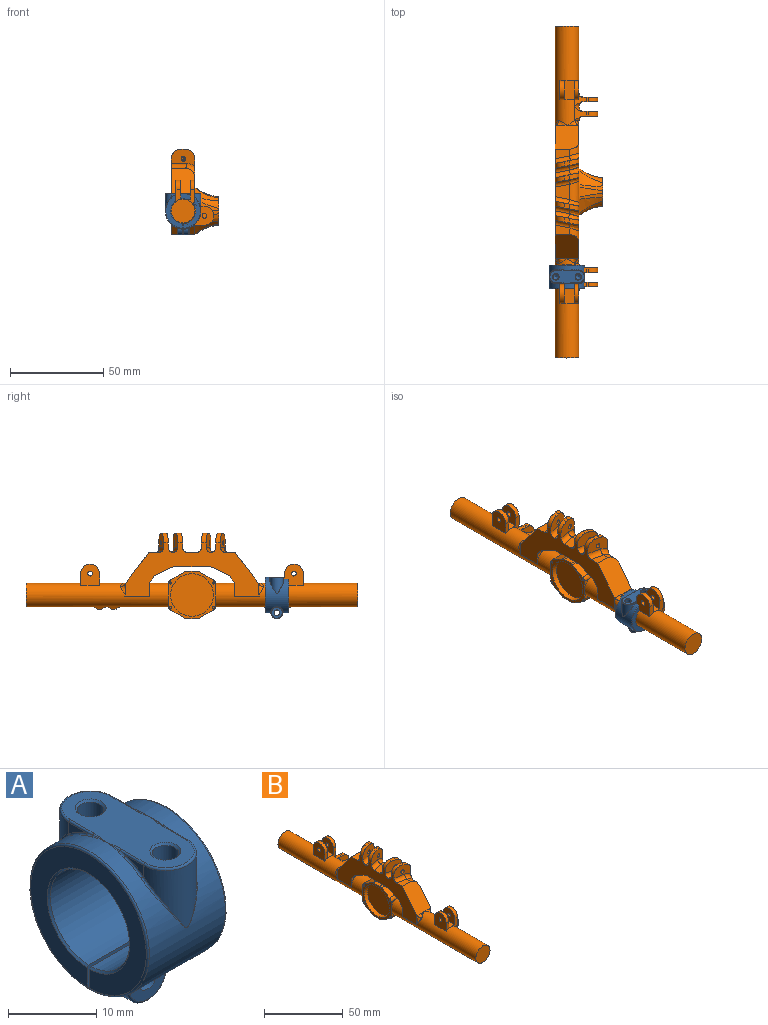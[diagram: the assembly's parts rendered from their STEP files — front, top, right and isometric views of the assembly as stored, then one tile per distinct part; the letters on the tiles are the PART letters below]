
ASSEMBLY  parts=2 mates=1
PART A: 89 faces, bbox 12.8x20.7x23.4 mm
  f0: cylinder r=9.53mm len=19.05mm, axis (-1,0,0), area 459.6mm2, adj f16,f17,f24,f25,f26,f27,f28,f29
  f1: cylinder r=6.35mm len=12.7mm, axis (-1,0,0), area 481.6mm2, adj f16,f17,f50,f51
  f2: cylinder r=1.5mm len=3mm, axis (0,1,0), area 28.1mm2, adj f10,f17
  f3: plane 18.54x18.54mm, normal (1,0,0), area 132mm2, adj f16,f17,f25,f51
  f4: plane 0.71x0.19mm, normal (-1,0,0), area 0.1mm2, adj f6,f20,f48
  f5: plane 0.71x0.19mm, normal (1,0,0), area 0.1mm2, adj f6,f18,f40
  f6: cylinder r=3.17mm len=6.35mm, axis (0,1,0), area 26.7mm2, adj f4,f5,f17,f19,f39,f49
  f7: cylinder r=1.5mm len=3mm, axis (0,1,0), area 28.1mm2, adj f9,f16
  f8: plane 18.54x18.54mm, normal (-1,0,0), area 132mm2, adj f16,f17,f24,f50
  f9: plane 5.84x5.84mm, normal (0,-1,0), area 19.8mm2, adj f7,f21,f22,f23,f32,f33,f34
  f10: plane 5.84x5.84mm, normal (0,1,0), area 19.8mm2, adj f2,f18,f19,f20,f43,f44,f45
  f11: cylinder r=3.17mm len=6.35mm, axis (0,1,0), area 26.7mm2, adj f12,f13,f16,f22,f28,f38
  f12: plane 0.71x0.19mm, normal (-1,0,0), area 0.1mm2, adj f11,f23,f29
  f13: plane 0.71x0.19mm, normal (1,0,0), area 0.1mm2, adj f11,f21,f37
  f14: cylinder r=3.17mm len=6.12mm, axis (0,-1,0), area 21mm2, adj f27,f44
  f15: cylinder r=3.17mm len=6.12mm, axis (0,1,0), area 21mm2, adj f26,f33
  f16: plane 12.71x6.36mm, normal (0,1,0), area 49mm2, adj f0,f1,f3,f7,f8,f11,f24,f25
  f17: plane 12.71x6.36mm, normal (0,-1,0), area 49mm2, adj f0,f1,f2,f3,f6,f8,f24,f25
  f18: cylinder r=0.25mm len=0.57mm, axis (0,0,-1), area 0.1mm2, adj f5,f10,f19,f41,f42
  f19: torus R=2.92mm, axis (0,-1,0), area 3.9mm2, adj f6,f10,f18,f20
  f20: cylinder r=0.25mm len=0.57mm, axis (0,0,1), area 0.1mm2, adj f4,f10,f19,f46,f47
  f21: cylinder r=0.25mm len=0.57mm, axis (0,0,1), area 0.1mm2, adj f9,f13,f22,f35,f36
  f22: torus R=2.92mm, axis (0,-1,0), area 3.9mm2, adj f9,f11,f21,f23
  f23: cylinder r=0.25mm len=0.57mm, axis (0,0,-1), area 0.1mm2, adj f9,f12,f22,f30,f31
  f24: torus R=9.27mm, axis (1,0,0), area 23.5mm2, adj f0,f8,f16,f17
  f25: torus R=9.27mm, axis (-1,0,0), area 23.5mm2, adj f0,f3,f16,f17
  f26: bspline ~6.77x5.02mm, area 3.3mm2, adj f0,f15,f31,f32,f34,f35
  f27: bspline ~6.77x5.02mm, area 3.3mm2, adj f0,f14,f42,f43,f45,f46
  f28: bspline ~3.57x0.71mm, area 0.8mm2, adj f0,f11,f16,f29
  f29: torus R=9.78mm, axis (-1,0,0), area 0.3mm2, adj f0,f12,f28,f30
  f30: bspline ~0.39x0.37mm, area 0.1mm2, adj f0,f23,f29,f31
  f31: bspline ~0.47x0.45mm, area 0.1mm2, adj f23,f26,f30,f32
  f32: bspline ~0.38x0.33mm, area 0.1mm2, adj f9,f26,f31,f33
  f33: torus R=2.92mm, axis (0,-1,0), area 3.2mm2, adj f9,f15,f32,f34
  f34: bspline ~0.38x0.35mm, area 0.1mm2, adj f9,f26,f33,f35
  f35: bspline ~0.49x0.46mm, area 0.1mm2, adj f21,f26,f34,f36
  f36: bspline ~0.41x0.38mm, area 0.1mm2, adj f0,f21,f35,f37
  f37: torus R=9.78mm, axis (-1,0,0), area 0.3mm2, adj f0,f13,f36,f38
  f38: bspline ~3.57x0.71mm, area 0.8mm2, adj f0,f11,f16,f37
  f39: bspline ~3.57x0.71mm, area 0.8mm2, adj f0,f6,f17,f40
  f40: torus R=9.78mm, axis (-1,0,0), area 0.3mm2, adj f0,f5,f39,f41
  f41: bspline ~0.39x0.37mm, area 0.1mm2, adj f0,f18,f40,f42
  f42: bspline ~0.47x0.45mm, area 0.1mm2, adj f18,f27,f41,f43
  f43: bspline ~0.38x0.35mm, area 0.1mm2, adj f10,f27,f42,f44
  f44: torus R=2.92mm, axis (0,-1,0), area 3.2mm2, adj f10,f14,f43,f45
  f45: bspline ~0.38x0.33mm, area 0.1mm2, adj f10,f27,f44,f46
  f46: bspline ~0.49x0.46mm, area 0.1mm2, adj f20,f27,f45,f47
  f47: bspline ~0.41x0.38mm, area 0.1mm2, adj f0,f20,f46,f48
  f48: torus R=9.78mm, axis (-1,0,0), area 0.3mm2, adj f0,f4,f47,f49
  f49: bspline ~3.57x0.71mm, area 0.8mm2, adj f0,f6,f17,f48
  f50: cone r=6.35mm half-angle=45deg, axis (-1,0,0), area 14.5mm2, adj f1,f8,f16,f17
  f51: cone r=6.6mm half-angle=45deg, axis (1,0,0), area 14.5mm2, adj f1,f3,f16,f17
  f52: plane 2.89x1.55mm, normal (1,0,0), area 1.9mm2, adj f53,f62,f80
  f53: cylinder r=3.5mm len=8.58mm, axis (0,0,1), area 53.7mm2, adj f52,f54,f63,f79
  f54: plane 2.89x1.55mm, normal (-1,0,0), area 1.9mm2, adj f53,f61,f78
  f55: cylinder r=3.5mm len=8.58mm, axis (0,0,1), area 53.7mm2, adj f56,f57,f66,f72
  f56: plane 2.89x1.55mm, normal (-1,0,0), area 1.9mm2, adj f55,f65,f73
  f57: plane 2.89x1.55mm, normal (1,0,0), area 1.9mm2, adj f55,f67,f71
  f58: plane 18.58x7.09mm, normal (0,0,1), area 92.5mm2, adj f59,f60,f61,f62,f63,f64,f65,f66
  f59: bspline ~2.28x0.28mm, area 0.2mm2, adj f58,f61,f76
  f60: bspline ~2.28x0.28mm, area 0.2mm2, adj f58,f62,f82
  f61: cylinder r=0.25mm len=3.82mm, axis (0,-1,0), area 1.5mm2, adj f54,f58,f59,f63,f77
  f62: cylinder r=0.25mm len=3.82mm, axis (0,1,0), area 1.5mm2, adj f52,f58,f60,f63,f81
  f63: torus R=3.25mm, axis (0,0,1), area 4.3mm2, adj f53,f58,f61,f62
  f64: bspline ~2.28x0.28mm, area 0.2mm2, adj f58,f65,f75
  f65: cylinder r=0.25mm len=3.82mm, axis (0,-1,0), area 1.5mm2, adj f56,f58,f64,f66,f74
  f66: torus R=3.25mm, axis (0,0,1), area 4.3mm2, adj f55,f58,f65,f67
  f67: cylinder r=0.25mm len=3.82mm, axis (0,1,0), area 1.5mm2, adj f57,f58,f66,f68,f70
  f68: bspline ~2.28x0.28mm, area 0.2mm2, adj f58,f67,f69
  f69: bspline ~2.19x0.24mm, area 0.2mm2, adj f0,f68,f70
  f70: bspline ~1.88x0.52mm, area 0.3mm2, adj f0,f67,f69,f71
  f71: torus R=9.78mm, axis (1,0,0), area 1.3mm2, adj f0,f57,f70,f72
  f72: bspline ~7.61x7.51mm, area 3.8mm2, adj f0,f55,f71,f73
  f73: torus R=9.78mm, axis (1,0,0), area 1.3mm2, adj f0,f56,f72,f74
  f74: bspline ~2.13x0.61mm, area 0.3mm2, adj f0,f65,f73,f75
  f75: bspline ~2.19x0.24mm, area 0.3mm2, adj f0,f64,f74
  f76: bspline ~2.36x0.28mm, area 0.2mm2, adj f0,f59,f77
  f77: bspline ~2.13x0.61mm, area 0.3mm2, adj f0,f61,f76,f78
  f78: torus R=9.78mm, axis (1,0,0), area 1.3mm2, adj f0,f54,f77,f79
  f79: bspline ~7.61x7.51mm, area 3.8mm2, adj f0,f53,f78,f80
  f80: torus R=9.78mm, axis (1,0,0), area 1.3mm2, adj f0,f52,f79,f81
  f81: bspline ~1.88x0.52mm, area 0.3mm2, adj f0,f62,f80,f82
  f82: bspline ~2.53x0.33mm, area 0.2mm2, adj f0,f60,f81
  f83: cone r=0mm half-angle=59deg, axis (0,0,1), area 8.2mm2, adj f84
  f84: cylinder r=1.5mm len=3mm, axis (0,0,1), area 27.5mm2, adj f83,f88
  f85: cone r=0mm half-angle=59deg, axis (0,0,1), area 8.2mm2, adj f86
  f86: cylinder r=1.5mm len=3mm, axis (0,0,1), area 27.5mm2, adj f85,f87
  f87: cone r=1.5mm half-angle=45deg, axis (0,0,1), area 3.7mm2, adj f58,f86
  f88: cone r=1.5mm half-angle=45deg, axis (0,0,1), area 3.7mm2, adj f58,f84
PART B: 219 faces, bbox 28.6x179.7x47.6 mm
  f0: cylinder r=6.35mm len=76.2mm, axis (0,-1,0), area 2387mm2, adj f1,f2,f3,f10,f24,f25,f26,f30
  f1: plane 7.45x6.35mm, normal (0,-1,0), area 19.1mm2, adj f0,f10,f195,f203,f204,f205,f213
  f2: plane 7.62x6.35mm, normal (0,1,0), area 19.2mm2, adj f0,f195,f203,f204,f205,f213
  f3: plane 6.35x3.81mm, normal (0,1,0), area 14.4mm2, adj f0,f194,f202,f204,f207
  f4: plane 7.45x6.35mm, normal (0,1,0), area 19.1mm2, adj f7,f8,f198,f200,f201,f206,f214
  f5: plane 6.35x3.81mm, normal (0,1,0), area 14.4mm2, adj f7,f197,f199,f201,f208
  f6: plane 7.62x6.35mm, normal (0,-1,0), area 19.2mm2, adj f7,f198,f200,f201,f206,f214
  f7: cylinder r=6.35mm len=76.2mm, axis (0,-1,0), area 2387mm2, adj f4,f5,f6,f8,f9,f21,f22,f23
  f8: cylinder r=10.16mm len=6.49mm, axis (0,-1,0), area 24.3mm2, adj f4,f7,f9,f124,f125,f126,f191,f214
  f9: torus R=8.89mm, axis (0,-1,0), area 54.5mm2, adj f7,f8,f126,f141,f214
  f10: cylinder r=10.16mm len=6.49mm, axis (0,-1,0), area 24.3mm2, adj f0,f1,f131,f133,f134,f188,f189,f213
  f11: plane 7.62x1.53mm, normal (0,0,1), area 0mm2, adj f78,f150,f180,f184
  f12: plane 7.62x5.14mm, normal (0,0,1), area 33.4mm2, adj f78,f89,f153,f172
  f13: plane 7.62x1.53mm, normal (0,0,1), area 0mm2, adj f78,f152,f176,f186
  f14: plane 7.62x5.14mm, normal (0,0,1), area 33.4mm2, adj f78,f88,f151,f174
  f15: plane 8.13x7.62mm, normal (0,0,1), area 50.3mm2, adj f78,f149,f178,f182
  f16: cylinder r=0.64mm len=5.08mm, axis (-1,0,0), area 9.3mm2, adj f20,f63,f71
  f17: cylinder r=0.64mm len=5.08mm, axis (-1,0,0), area 9.3mm2, adj f20,f64,f70
  f18: cylinder r=0.64mm len=5.08mm, axis (-1,0,0), area 9.3mm2, adj f20,f65,f69
  f19: cylinder r=0.64mm len=5.08mm, axis (-1,0,0), area 9.3mm2, adj f20,f66,f68
  f20: plane 25.4x25.4mm, normal (-1,0,0), area 129.2mm2, adj f16,f17,f18,f19,f21,f22,f24,f25
  f21: plane 5.87x3.92mm, normal (0,-1,0), area 6.4mm2, adj f7,f20,f42
  f22: plane 5.87x3.92mm, normal (0,-1,0), area 6.4mm2, adj f7,f20,f35
  f23: plane 5.97x4.02mm, normal (0,-1,0), area 6.4mm2, adj f7,f35,f54
  f24: plane 5.87x3.92mm, normal (0,1,0), area 6.4mm2, adj f0,f20,f40
  f25: plane 5.87x3.92mm, normal (0,1,0), area 6.4mm2, adj f0,f20,f38
  f26: plane 5.93x3.98mm, normal (0,1,0), area 6.4mm2, adj f0,f38,f49
  f27: plane 12.72x5.47mm, normal (0,0,1), area 69.1mm2, adj f20,f39,f41,f59
  f28: plane 5.93x3.98mm, normal (0,-1,0), area 6.4mm2, adj f7,f42,f56
  f29: plane 12.72x5.47mm, normal (0,0,-1), area 69.1mm2, adj f20,f36,f37,f46
  f30: plane 5.97x4.02mm, normal (0,1,0), area 6.4mm2, adj f0,f40,f51
  f31: plane 12.82x7.56mm, normal (0,-0.5,0.87), area 109.1mm2, adj f20,f41,f42,f60
  f32: plane 12.79x7.53mm, normal (0,0.5,0.87), area 109.1mm2, adj f20,f39,f40,f55
  f33: plane 12.82x7.56mm, normal (0,0.5,-0.87), area 109.1mm2, adj f20,f37,f38,f45
  f34: plane 12.79x7.53mm, normal (0,-0.5,-0.87), area 109.1mm2, adj f20,f35,f36,f50
  f35: cylinder r=2.54mm len=12.7mm, axis (1,0,0), area 32.2mm2, adj f7,f20,f22,f23,f34,f52
  f36: cylinder r=2.54mm len=12.7mm, axis (1,0,0), area 16.9mm2, adj f20,f29,f34,f48
  f37: cylinder r=2.54mm len=12.7mm, axis (1,0,0), area 16.9mm2, adj f20,f29,f33,f44
  f38: cylinder r=2.54mm len=12.7mm, axis (-1,0,0), area 32.2mm2, adj f0,f20,f25,f26,f33,f47
  f39: cylinder r=2.54mm len=12.7mm, axis (-1,0,0), area 16.9mm2, adj f20,f27,f32,f57
  f40: cylinder r=2.54mm len=12.7mm, axis (-1,0,0), area 32.2mm2, adj f0,f20,f24,f30,f32,f53
  f41: cylinder r=2.54mm len=12.7mm, axis (-1,0,0), area 16.9mm2, adj f20,f27,f31,f61
  f42: cylinder r=2.54mm len=12.7mm, axis (1,0,0), area 32.2mm2, adj f7,f20,f21,f28,f31,f58
  f43: plane 15.29x15.27mm, normal (1,0,0), area 136.8mm2, adj f44,f45,f46,f47,f48,f49,f50,f51
  f44: bspline ~12.7x5.81mm, area 24.7mm2, adj f37,f43,f45,f46
  f45: bspline ~12.7x8.64mm, area 72.1mm2, adj f33,f43,f44,f47
  f46: bspline ~12.7x5.44mm, area 45.7mm2, adj f29,f43,f44,f48
  f47: bspline ~12.7x7.77mm, area 48.9mm2, adj f38,f43,f45,f49
  f48: bspline ~12.7x5.81mm, area 24.7mm2, adj f36,f43,f46,f50
  f49: bspline ~12.7x5.87mm, area 49.3mm2, adj f26,f43,f47,f51
  f50: bspline ~12.7x8.64mm, area 72.1mm2, adj f34,f43,f48,f52
  f51: bspline ~12.7x5.87mm, area 49.3mm2, adj f30,f43,f49,f53
  f52: bspline ~12.7x7.77mm, area 48.9mm2, adj f35,f43,f50,f54
  f53: bspline ~12.7x7.77mm, area 48.9mm2, adj f40,f43,f51,f55
  f54: bspline ~12.7x5.87mm, area 49.3mm2, adj f23,f43,f52,f56
  f55: bspline ~12.7x8.64mm, area 72.1mm2, adj f32,f43,f53,f57
  f56: bspline ~12.7x5.87mm, area 49.3mm2, adj f28,f43,f54,f58
  f57: bspline ~12.7x5.81mm, area 24.7mm2, adj f39,f43,f55,f59
  f58: bspline ~12.7x7.77mm, area 48.9mm2, adj f42,f43,f56,f60
  f59: bspline ~12.7x5.44mm, area 45.7mm2, adj f27,f43,f57,f61
  f60: bspline ~12.7x8.64mm, area 72.1mm2, adj f31,f43,f58,f61
  f61: bspline ~12.7x5.81mm, area 24.7mm2, adj f41,f43,f59,f60
  f62: cylinder r=3.81mm len=7.62mm, axis (1,0,0), area 121.6mm2, adj f43,f215
  f63: plane 1.26x1.1mm, normal (-1,0,0), area 1.1mm2, adj f16,f71
  f64: plane 1.26x1.1mm, normal (-1,0,0), area 1.1mm2, adj f17,f70
  f65: plane 1.26x1.1mm, normal (-1,0,0), area 1.1mm2, adj f18,f69
  f66: plane 1.26x1.1mm, normal (-1,0,0), area 1.1mm2, adj f19,f68
  f67: cylinder r=11.43mm len=22.86mm, axis (-1,0,0), area 220.7mm2, adj f20,f216
  f68: cylinder r=0.64mm len=5.08mm, axis (-1,0,0), area 9.3mm2, adj f19,f20,f66
  f69: cylinder r=0.64mm len=5.08mm, axis (-1,0,0), area 9.3mm2, adj f18,f20,f65
  f70: cylinder r=0.64mm len=5.08mm, axis (-1,0,0), area 9.3mm2, adj f17,f20,f64
  f71: cylinder r=0.64mm len=5.08mm, axis (-1,0,0), area 9.3mm2, adj f16,f20,f63
  f72: plane 0.13x0.13mm, normal (0,1,0), area 0mm2, adj f78,f88,f164
  f73: plane 0.13x0.13mm, normal (0,1,0), area 0mm2, adj f79,f88,f161
  f74: plane 0.64x0.03mm, normal (0,-1,0), area 0mm2, adj f0,f78,f94
  f75: plane 6.35x6.35mm, normal (0,-1,0), area 8.7mm2, adj f0,f78,f87
  f76: plane 6.35x6.35mm, normal (0,-1,0), area 8.7mm2, adj f0,f79,f87
  f77: plane 13.25x0.11mm, normal (0,0,-1), area 0.4mm2, adj f0,f79,f93,f156
  f78: plane 73.11x30.44mm, normal (-1,0,0), area 891.6mm2, adj f11,f12,f13,f14,f15,f72,f74,f75
  f79: plane 72.3x29.63mm, normal (1,0,0), area 722.1mm2, adj f73,f76,f77,f82,f84,f85,f86,f87
  f80: plane 0.64x0.03mm, normal (0,1,0), area 0mm2, adj f7,f78,f92
  f81: plane 6.35x6.35mm, normal (0,1,0), area 8.7mm2, adj f7,f78,f90
  f82: plane 6.35x6.35mm, normal (0,1,0), area 8.7mm2, adj f7,f79,f90
  f83: plane 0.13x0.13mm, normal (0,-1,0), area 0mm2, adj f78,f89,f170
  f84: plane 0.13x0.13mm, normal (0,-1,0), area 0mm2, adj f79,f89,f167
  f85: plane 13.25x0.11mm, normal (0,0,-1), area 0.4mm2, adj f7,f79,f91,f158
  f86: plane 19.47x12.7mm, normal (0,0,-1), area 247.2mm2, adj f78,f79,f95,f96
  f87: plane 12.7x3.86mm, normal (0,-0.79,-0.61), area 61.8mm2, adj f75,f76,f78,f79,f95
  f88: plane 18.38x14.57mm, normal (0,0.79,0.61), area 257.5mm2, adj f14,f72,f73,f78,f79,f151,f162,f163
  f89: plane 18.38x14.57mm, normal (0,-0.79,0.61), area 257.5mm2, adj f12,f78,f79,f83,f84,f153,f168,f169
  f90: plane 12.7x3.86mm, normal (0,0.79,-0.61), area 61.8mm2, adj f78,f79,f81,f82,f96
  f91: plane 0.64x0.03mm, normal (0,1,0), area 0mm2, adj f7,f79,f85
  f92: plane 13.25x0.11mm, normal (0,0,-1), area 0.4mm2, adj f7,f78,f80,f159
  f93: plane 0.64x0.03mm, normal (0,-1,0), area 0mm2, adj f0,f77,f79
  f94: plane 13.25x0.11mm, normal (0,0,-1), area 0.4mm2, adj f0,f74,f78,f157
  f95: plane 12.7x10.22mm, normal (0,-0.44,-0.9), area 144.7mm2, adj f78,f79,f86,f87
  f96: plane 12.7x10.22mm, normal (0,0.44,-0.9), area 144.7mm2, adj f78,f79,f86,f90
  f97: plane 13.13x10.54mm, normal (0.2,-0.98,0), area 87.3mm2, adj f78,f79,f99,f109,f110,f118,f178,f179
  f98: plane 13.13x9.65mm, normal (-0.2,0.98,0), area 85.3mm2, adj f78,f79,f99,f109,f110,f118,f176,f177
  f99: plane 3.05x2.54mm, normal (0,0,1), area 6.5mm2, adj f97,f98,f109,f110
  f100: plane 13.13x9.65mm, normal (-0.2,0.98,0), area 85.3mm2, adj f78,f79,f102,f115,f116,f117,f174,f175
  f101: plane 13.13x10.54mm, normal (0.2,-0.98,0), area 87.3mm2, adj f78,f79,f102,f115,f116,f117,f186,f187
  f102: plane 3.05x2.54mm, normal (0,0,1), area 6.5mm2, adj f100,f101,f115,f116
  f103: plane 13.13x9.65mm, normal (-0.2,-0.98,0), area 85.3mm2, adj f78,f79,f105,f113,f114,f144,f172,f173
  f104: plane 13.13x10.54mm, normal (0.2,0.98,0), area 87.3mm2, adj f78,f79,f105,f113,f114,f144,f184,f185
  f105: plane 3.05x2.54mm, normal (0,0,1), area 6.5mm2, adj f103,f104,f113,f114
  f106: plane 13.13x10.54mm, normal (0.2,0.98,0), area 87.3mm2, adj f78,f79,f108,f111,f112,f143,f182,f183
  f107: plane 13.13x9.65mm, normal (-0.2,-0.98,0), area 85.3mm2, adj f78,f79,f108,f111,f112,f143,f180,f181
  f108: plane 3.05x2.54mm, normal (0,0,1), area 6.5mm2, adj f106,f107,f111,f112
  f109: cylinder r=5.08mm len=5.08mm, axis (0,1,0), area 20.3mm2, adj f79,f97,f98,f99
  f110: cylinder r=5.08mm len=5.08mm, axis (0,-1,0), area 20.3mm2, adj f78,f97,f98,f99
  f111: cylinder r=5.08mm len=5.08mm, axis (0,-1,0), area 20.3mm2, adj f78,f106,f107,f108
  f112: cylinder r=5.08mm len=5.08mm, axis (0,1,0), area 20.3mm2, adj f79,f106,f107,f108
  f113: cylinder r=5.08mm len=5.08mm, axis (0,1,0), area 20.3mm2, adj f79,f103,f104,f105
  f114: cylinder r=5.08mm len=5.08mm, axis (0,-1,0), area 20.3mm2, adj f78,f103,f104,f105
  f115: cylinder r=5.08mm len=5.08mm, axis (0,-1,0), area 20.3mm2, adj f78,f100,f101,f102
  f116: cylinder r=5.08mm len=5.08mm, axis (0,1,0), area 20.3mm2, adj f79,f100,f101,f102
  f117: cylinder r=1.27mm len=2.98mm, axis (-0.2,0.98,0), area 19.9mm2, adj f100,f101
  f118: cylinder r=1.27mm len=2.98mm, axis (-0.2,0.98,0), area 19.9mm2, adj f97,f98
  f119: plane 3.57x2.54mm, normal (0,0,-1), area 9.1mm2, adj f120,f122,f138,f142
  f120: plane 11.69x10.38mm, normal (0,1,0), area 71.2mm2, adj f119,f121,f138,f142,f146,f155,f192
  f121: plane 2.54x0.88mm, normal (0,0,1), area 2.2mm2, adj f120,f122,f138,f155
  f122: plane 11.69x10.38mm, normal (0,-1,0), area 71.2mm2, adj f119,f121,f138,f142,f146,f155,f191
  f123: plane 3.57x2.54mm, normal (0,0,-1), area 9.1mm2, adj f124,f126,f137,f141
  f124: plane 11.69x10.38mm, normal (0,1,0), area 71.2mm2, adj f8,f123,f125,f137,f141,f145,f191
  f125: plane 2.54x0.88mm, normal (0,0,1), area 2.2mm2, adj f8,f124,f126,f137
  f126: plane 11.69x10.38mm, normal (0,-1,0), area 71.2mm2, adj f8,f9,f123,f125,f137,f141,f145
  f127: plane 3.57x2.54mm, normal (0,0,-1), area 9.1mm2, adj f128,f130,f136,f140
  f128: plane 11.69x10.38mm, normal (0,1,0), area 71.2mm2, adj f127,f129,f136,f140,f148,f154,f188
  f129: plane 2.54x0.88mm, normal (0,0,1), area 2.2mm2, adj f128,f130,f136,f154
  f130: plane 11.69x10.38mm, normal (0,-1,0), area 71.2mm2, adj f127,f129,f136,f140,f148,f154,f190
  f131: plane 11.69x10.38mm, normal (0,-1,0), area 71.2mm2, adj f10,f132,f134,f135,f139,f147,f188
  f132: plane 3.57x2.54mm, normal (0,0,-1), area 9.1mm2, adj f131,f133,f135,f139
  f133: plane 11.69x10.38mm, normal (0,1,0), area 71.2mm2, adj f10,f132,f134,f135,f139,f147,f189
  f134: plane 2.54x0.88mm, normal (0,0,1), area 2.2mm2, adj f10,f131,f133,f135
  f135: cylinder r=5.08mm len=10.16mm, axis (0,1,0), area 40.5mm2, adj f131,f132,f133,f134
  f136: cylinder r=5.08mm len=10.16mm, axis (0,-1,0), area 40.5mm2, adj f127,f128,f129,f130
  f137: cylinder r=5.08mm len=10.16mm, axis (0,-1,0), area 40.5mm2, adj f123,f124,f125,f126
  f138: cylinder r=5.08mm len=10.16mm, axis (0,-1,0), area 40.5mm2, adj f119,f120,f121,f122
  f139: cylinder r=30.48mm len=9.13mm, axis (0,-1,0), area 39.4mm2, adj f0,f131,f132,f133,f188,f189
  f140: cylinder r=30.48mm len=9.13mm, axis (0,-1,0), area 39.4mm2, adj f0,f127,f128,f130,f188,f190
  f141: cylinder r=30.48mm len=9.13mm, axis (0,-1,0), area 39.4mm2, adj f7,f9,f123,f124,f126,f191
  f142: cylinder r=30.48mm len=9.13mm, axis (0,-1,0), area 39.4mm2, adj f7,f119,f120,f122,f191,f192
  f143: cylinder r=1.27mm len=2.98mm, axis (-0.2,-0.98,0), area 19.9mm2, adj f106,f107
  f144: cylinder r=1.27mm len=2.98mm, axis (-0.2,-0.98,0), area 19.9mm2, adj f103,f104
  f145: cylinder r=1.27mm len=2.54mm, axis (0,-1,0), area 20.3mm2, adj f124,f126
  f146: cylinder r=1.27mm len=2.54mm, axis (0,-1,0), area 20.3mm2, adj f120,f122
  f147: cylinder r=1.27mm len=2.54mm, axis (0,1,0), area 20.3mm2, adj f131,f133
  f148: cylinder r=1.27mm len=2.54mm, axis (0,1,0), area 20.3mm2, adj f128,f130
  f149: cylinder r=5.08mm len=11.16mm, axis (0,-1,0), area 77mm2, adj f15,f79,f179,f183
  f150: cylinder r=5.08mm len=5.08mm, axis (0,-1,0), area 0mm2, adj f11,f79,f181,f185
  f151: cylinder r=5.08mm len=7.53mm, axis (0,-1,0), area 38.4mm2, adj f14,f79,f88,f175
  f152: cylinder r=5.08mm len=5.08mm, axis (0,-1,0), area 0mm2, adj f13,f79,f177,f187
  f153: cylinder r=5.08mm len=7.53mm, axis (0,-1,0), area 38.4mm2, adj f12,f79,f89,f173
  f154: cylinder r=10.16mm len=7.61mm, axis (0,-1,0), area 27.1mm2, adj f0,f128,f129,f130,f162,f188,f190
  f155: cylinder r=10.16mm len=7.61mm, axis (0,-1,0), area 27.1mm2, adj f7,f120,f121,f122,f168,f191,f192
  f156: bspline ~1.43x0.76mm, area 0.1mm2, adj f0,f77,f79
  f157: bspline ~1.43x0.76mm, area 0.1mm2, adj f0,f78,f94
  f158: bspline ~1.43x0.76mm, area 0.1mm2, adj f7,f79,f85
  f159: bspline ~1.43x0.76mm, area 0.1mm2, adj f7,f78,f92
  f160: bspline ~6.22x2.54mm, area 9.8mm2, adj f0,f79,f161,f190
  f161: torus R=8.89mm, axis (0,-1,0), area 0.6mm2, adj f73,f160,f162,f190
  f162: bspline ~6.41x2.66mm, area 9.8mm2, adj f0,f88,f154,f161,f190
  f163: bspline ~6.22x2.54mm, area 6.4mm2, adj f0,f88,f164
  f164: torus R=8.89mm, axis (0,-1,0), area 0.6mm2, adj f0,f72,f163,f165
  f165: bspline ~6.22x2.54mm, area 6.4mm2, adj f0,f78,f164
  f166: bspline ~6.22x2.54mm, area 9.8mm2, adj f7,f79,f167,f192
  f167: torus R=8.89mm, axis (0,-1,0), area 0.6mm2, adj f84,f166,f168,f192
  f168: bspline ~6.41x2.66mm, area 9.8mm2, adj f7,f89,f155,f167,f192
  f169: bspline ~6.22x2.54mm, area 6.4mm2, adj f7,f89,f170
  f170: torus R=8.89mm, axis (0,-1,0), area 0.6mm2, adj f7,f83,f169,f171
  f171: bspline ~6.22x2.54mm, area 6.4mm2, adj f7,f78,f170
  f172: cylinder r=2.49mm len=8.6mm, axis (-0.98,0.2,0), area 31.4mm2, adj f12,f78,f103,f173
  f173: bspline ~8.94x7.57mm, area 27.1mm2, adj f79,f103,f153,f172
  f174: cylinder r=2.49mm len=8.6mm, axis (0.98,0.2,0), area 31.4mm2, adj f14,f78,f100,f175
  f175: bspline ~8.94x8.88mm, area 27.1mm2, adj f79,f100,f151,f174
  f176: cylinder r=2.49mm len=8.6mm, axis (0.98,0.2,0), area 31.4mm2, adj f13,f78,f98,f177
  f177: bspline ~8.94x7.9mm, area 27.1mm2, adj f79,f98,f152,f176
  f178: cylinder r=2.49mm len=8.11mm, axis (-0.98,-0.2,0), area 29.4mm2, adj f15,f78,f97,f179
  f179: bspline ~7.57x7.57mm, area 26.4mm2, adj f79,f97,f149,f178
  f180: cylinder r=2.49mm len=8.6mm, axis (-0.98,0.2,0), area 31.4mm2, adj f11,f78,f107,f181
  f181: bspline ~8.94x7.57mm, area 27.1mm2, adj f79,f107,f150,f180
  f182: cylinder r=2.49mm len=8.11mm, axis (0.98,-0.2,0), area 29.4mm2, adj f15,f78,f106,f183
  f183: bspline ~7.57x7.57mm, area 26.4mm2, adj f79,f106,f149,f182
  f184: cylinder r=2.49mm len=8.11mm, axis (0.98,-0.2,0), area 29.4mm2, adj f11,f78,f104,f185
  f185: bspline ~7.57x7.57mm, area 26.4mm2, adj f79,f104,f150,f184
  f186: cylinder r=2.49mm len=8.11mm, axis (-0.98,-0.2,0), area 29.4mm2, adj f13,f78,f101,f187
  f187: bspline ~7.57x7.57mm, area 26.4mm2, adj f79,f101,f152,f186
  f188: torus R=8.89mm, axis (0,-1,0), area 112.6mm2, adj f10,f128,f131,f139,f140,f154
  f189: torus R=8.89mm, axis (0,-1,0), area 54.5mm2, adj f0,f10,f133,f139,f213
  f190: torus R=8.89mm, axis (0,-1,0), area 54.7mm2, adj f0,f130,f140,f154,f160,f161,f162
  f191: torus R=8.89mm, axis (0,-1,0), area 112.6mm2, adj f8,f122,f124,f141,f142,f155
  f192: torus R=8.89mm, axis (0,-1,0), area 54.7mm2, adj f7,f120,f142,f155,f166,f167,f168
  f193: plane 6.35x3.81mm, normal (0,-1,0), area 14.4mm2, adj f0,f194,f202,f204,f207
  f194: plane 11.43x10.16mm, normal (-1,0,0), area 100mm2, adj f0,f3,f193,f207,f210
  f195: plane 10.5x10.16mm, normal (1,0,0), area 90.5mm2, adj f1,f2,f205,f209,f213
  f196: plane 6.35x3.81mm, normal (0,-1,0), area 14.4mm2, adj f7,f197,f199,f201,f208
  f197: plane 11.43x10.16mm, normal (-1,0,0), area 100mm2, adj f5,f7,f196,f208,f212
  f198: plane 10.5x10.16mm, normal (1,0,0), area 90.5mm2, adj f4,f6,f206,f211,f214
  f199: plane 10.16x10.16mm, normal (1,0,0), area 87.1mm2, adj f5,f196,f201,f208,f212
  f200: plane 10.16x10.16mm, normal (-1,0,0), area 87.1mm2, adj f4,f6,f201,f206,f211
  f201: plane 10.16x5.08mm, normal (0,0,1), area 51.6mm2, adj f4,f5,f6,f196,f199,f200
  f202: plane 10.16x10.16mm, normal (1,0,0), area 87.1mm2, adj f3,f193,f204,f207,f210
  f203: plane 10.16x10.16mm, normal (-1,0,0), area 87.1mm2, adj f1,f2,f204,f205,f209
  f204: plane 10.16x5.08mm, normal (0,0,1), area 51.6mm2, adj f1,f2,f3,f193,f202,f203
  f205: cylinder r=5.08mm len=10.16mm, axis (1,0,0), area 40.5mm2, adj f1,f2,f195,f203
  f206: cylinder r=5.08mm len=10.16mm, axis (1,0,0), area 40.5mm2, adj f4,f6,f198,f200
  f207: cylinder r=5.08mm len=10.16mm, axis (-1,0,0), area 40.5mm2, adj f3,f193,f194,f202
  f208: cylinder r=5.08mm len=10.16mm, axis (-1,0,0), area 40.5mm2, adj f5,f196,f197,f199
  f209: cylinder r=1.27mm len=2.54mm, axis (1,0,0), area 20.3mm2, adj f195,f203
  f210: cylinder r=1.27mm len=2.54mm, axis (1,0,0), area 20.3mm2, adj f194,f202
  f211: cylinder r=1.27mm len=2.54mm, axis (1,0,0), area 20.3mm2, adj f198,f200
  f212: cylinder r=1.27mm len=2.54mm, axis (1,0,0), area 20.3mm2, adj f197,f199
  f213: cylinder r=2.54mm len=10.16mm, axis (0,-1,0), area 26mm2, adj f0,f1,f2,f10,f189,f195
  f214: cylinder r=2.54mm len=10.16mm, axis (0,-1,0), area 26mm2, adj f4,f6,f7,f8,f9,f198
  f215: plane 7.62x7.62mm, normal (1,0,0), area 45.6mm2, adj f62
  f216: plane 22.86x22.86mm, normal (-1,0,0), area 410.4mm2, adj f67
  f217: plane 12.7x12.7mm, normal (0,1,0), area 126.7mm2, adj f0
  f218: plane 12.7x12.7mm, normal (0,-1,0), area 126.7mm2, adj f7
PLACE A rot(axis=(0,0,1),90deg) t=(-11.36,-3.59,-11.03)mm
PLACE B t=(-107.62,-611.83,-113.9)mm
MATE fastened A.f0 <-> B.f0  axis (0,-1,0) through (-11.36,-48.94,-11.03)mm
